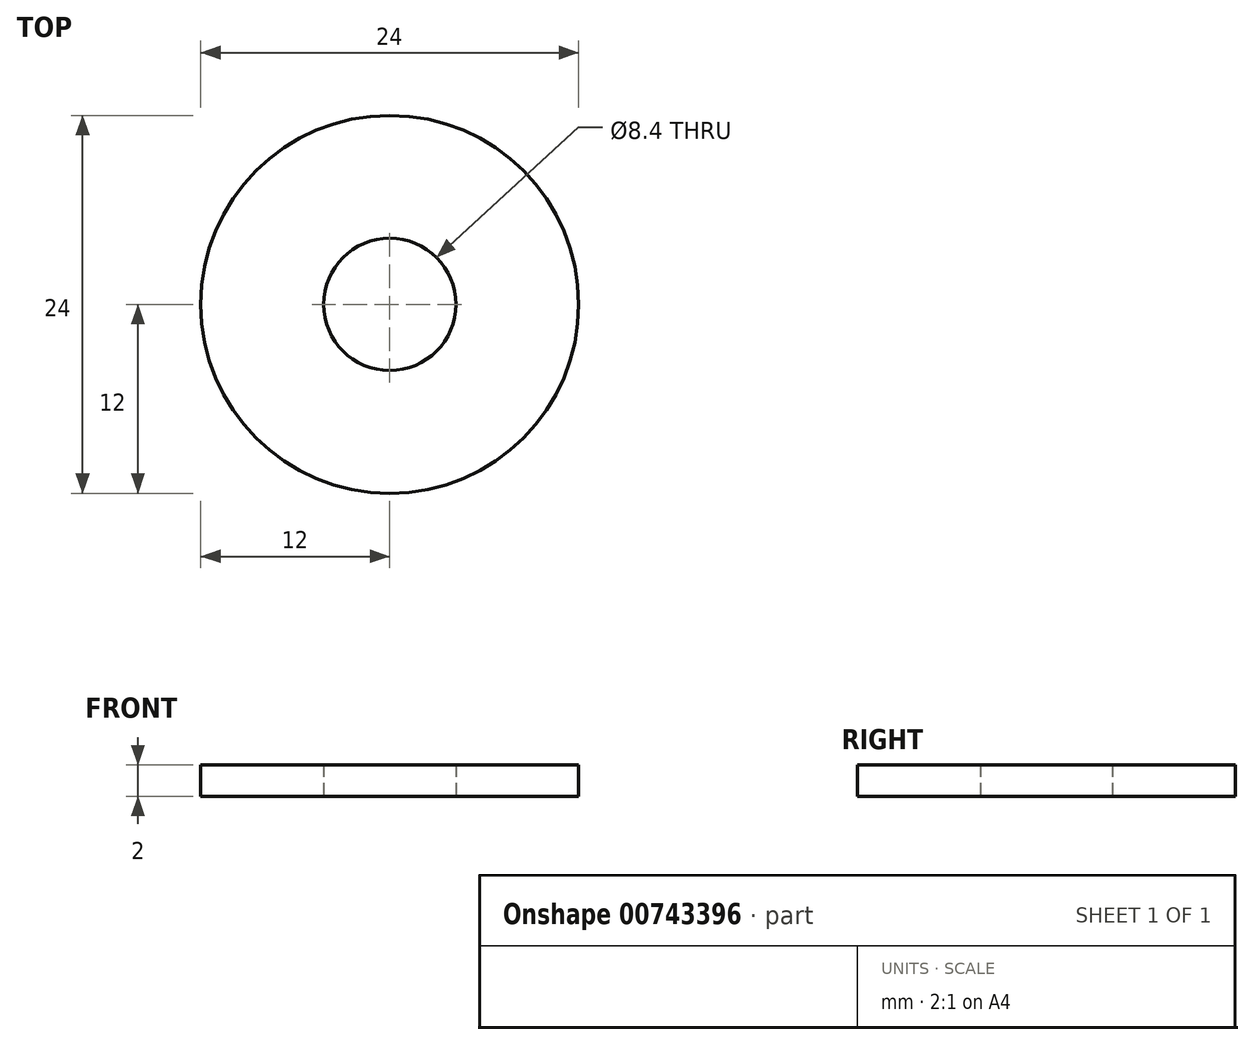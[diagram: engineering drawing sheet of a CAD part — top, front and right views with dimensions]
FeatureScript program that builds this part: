
annotation { "Feature Type Name" : "Feature", "Feature Type Description" : "" }
export const myFeature = defineFeature(function(context is Context, id is Id, definition is map)
    precondition{}
    {
        {
            var Q0;
            Q0=qCreatedBy(makeId("Top.planeOp"),FACE);
            var sketch = newSketch(context, id + "F0", { "sketchPlane" : qUnion([Q0])});
            skCircle(sketch, "E0", {"center": v(0, 0) * mm, "radius": 12 * mm});
            skCircle(sketch, "E1", {"center": v(0, 0) * mm, "radius": 4.2 * mm});
            skSolve(sketch);
        }
        {
            var Q0;
            Q0 = qSketchRegion(id + "F0", true);
            extrude(context, id + "F1", {"entities" : qUnion([Q0]), "depth" : 2 * mm, "offsetDistance" : 25 * mm});
        }
    });
